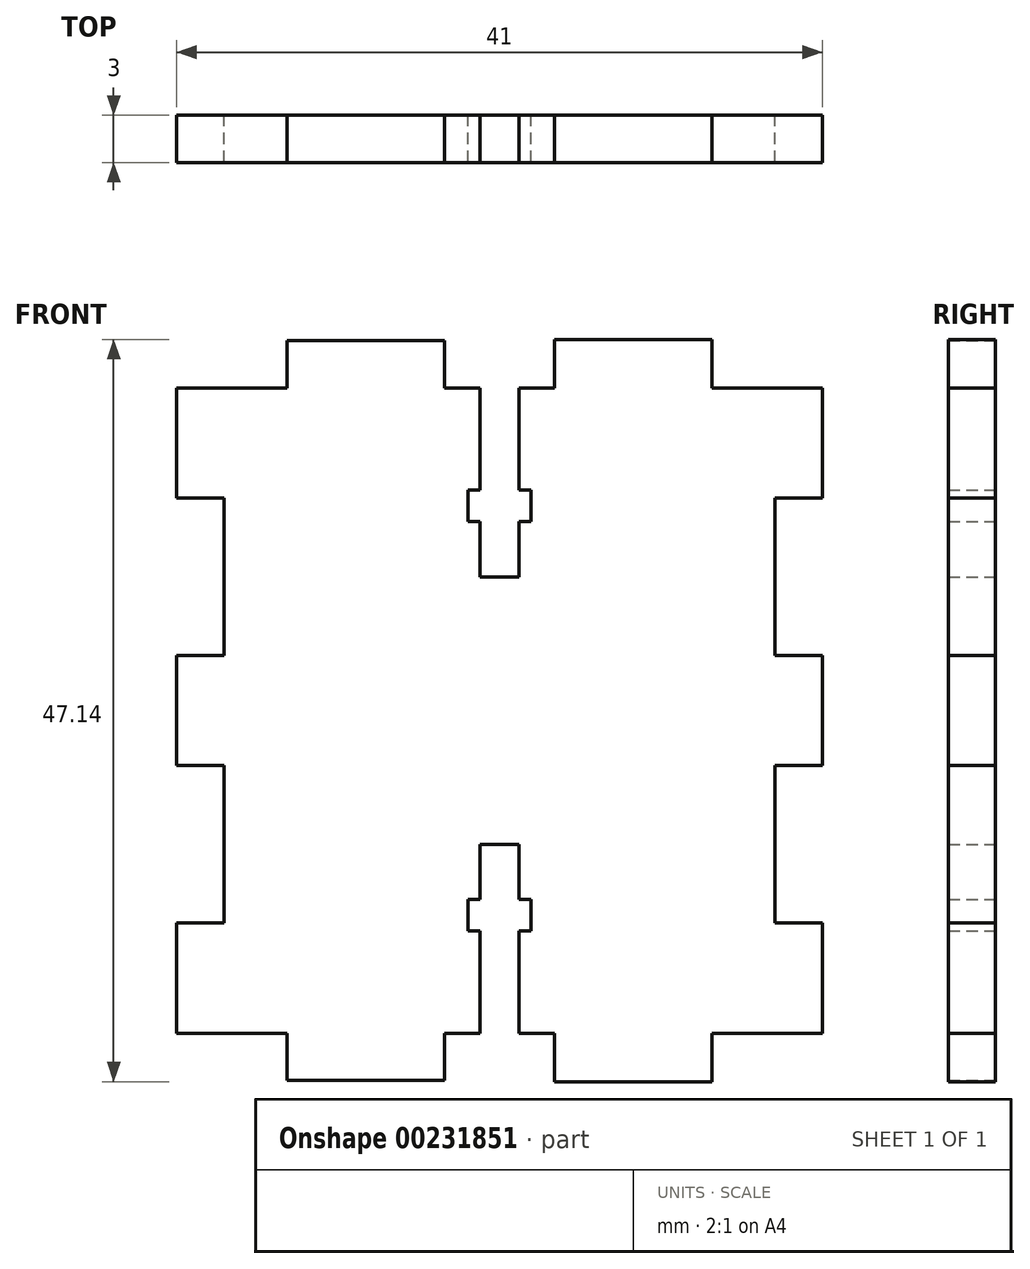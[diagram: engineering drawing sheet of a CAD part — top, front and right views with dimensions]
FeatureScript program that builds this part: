
annotation { "Feature Type Name" : "Feature", "Feature Type Description" : "" }
export const myFeature = defineFeature(function(context is Context, id is Id, definition is map)
    precondition{}
    {
        {
            var Q0;
            Q0=qCreatedBy(makeId("Front.planeOp"),FACE);
            var sketch = newSketch(context, id + "F0", { "sketchPlane" : qUnion([Q0])});
            skLineSegment(sketch, "E0", {"start": v(0, 0) * mm, "end": v(7, 0) * mm});
            skLineSegment(sketch, "E1", {"start": v(7, 0) * mm, "end": v(7, 3) * mm});
            skLineSegment(sketch, "E2", {"start": v(7, 3) * mm, "end": v(17, 3) * mm});
            skLineSegment(sketch, "E3", {"start": v(17, 3) * mm, "end": v(17, 0) * mm});
            skLineSegment(sketch, "E4", {"start": v(17, 0) * mm, "end": v(19.25, 0) * mm});
            skLineSegment(sketch, "E5", {"start": v(24, 0) * mm, "end": v(24, 3.07) * mm});
            skLineSegment(sketch, "E6", {"start": v(24, 3.07) * mm, "end": v(34, 3.07) * mm});
            skLineSegment(sketch, "E7", {"start": v(34, 3.07) * mm, "end": v(34, 0) * mm});
            skLineSegment(sketch, "E8", {"start": v(34, 0) * mm, "end": v(41, 0) * mm});
            skLineSegment(sketch, "E9", {"start": v(41, -20.5) * mm, "end": v(0, -20.5) * mm, "construction": true});
            skLineSegment(sketch, "E10.top", {"start": v(19.25, -12) * mm, "end": v(21.75, -12) * mm});
            skLineSegment(sketch, "E10.left", {"start": v(19.25, 0) * mm, "end": v(19.25, -6.5) * mm});
            skLineSegment(sketch, "E10.right", {"start": v(21.75, 0) * mm, "end": v(21.75, -6.5) * mm});
            skLineSegment(sketch, "E11.bottom", {"start": v(18.5, -8.5) * mm, "end": v(19.25, -8.5) * mm});
            skLineSegment(sketch, "E11.top", {"start": v(18.5, -6.5) * mm, "end": v(19.25, -6.5) * mm});
            skLineSegment(sketch, "E11.left", {"start": v(18.5, -8.5) * mm, "end": v(18.5, -6.5) * mm});
            skLineSegment(sketch, "E11.right", {"start": v(22.5, -8.5) * mm, "end": v(22.5, -6.5) * mm});
            skLineSegment(sketch, "E12.trimOffspring", {"start": v(21.75, -6.5) * mm, "end": v(22.5, -6.5) * mm});
            skLineSegment(sketch, "E13.trimOffspring", {"start": v(21.75, -8.5) * mm, "end": v(21.75, -12) * mm});
            skLineSegment(sketch, "E14.trimOffspring", {"start": v(19.25, -8.5) * mm, "end": v(19.25, -12) * mm});
            skLineSegment(sketch, "E15.trimOffspring", {"start": v(21.75, -8.5) * mm, "end": v(22.5, -8.5) * mm});
            skLineSegment(sketch, "E16.trimOffspring", {"start": v(21.75, 0) * mm, "end": v(24, 0) * mm});
            skLineSegment(sketch, "E17.MirrorCS", {"start": v(18.5, -34.5) * mm, "end": v(19.25, -34.5) * mm});
            skLineSegment(sketch, "E18.MirrorCS", {"start": v(22.5, -32.5) * mm, "end": v(22.5, -34.5) * mm});
            skLineSegment(sketch, "E19.MirrorCS", {"start": v(34, -44.07) * mm, "end": v(34, -41) * mm});
            skLineSegment(sketch, "E20.MirrorCS", {"start": v(17, -44) * mm, "end": v(17, -41) * mm});
            skLineSegment(sketch, "E21.MirrorCS", {"start": v(21.75, -41) * mm, "end": v(24, -41) * mm});
            skLineSegment(sketch, "E22.MirrorCS", {"start": v(19.25, -29) * mm, "end": v(21.75, -29) * mm});
            skLineSegment(sketch, "E23.MirrorCS", {"start": v(17, -41) * mm, "end": v(19.25, -41) * mm});
            skLineSegment(sketch, "E24.MirrorCS", {"start": v(24, -41) * mm, "end": v(24, -44.07) * mm});
            skLineSegment(sketch, "E25.MirrorCS", {"start": v(18.5, -32.5) * mm, "end": v(19.25, -32.5) * mm});
            skLineSegment(sketch, "E26.MirrorCS", {"start": v(7, -41) * mm, "end": v(7, -44) * mm});
            skLineSegment(sketch, "E27.MirrorCS", {"start": v(21.75, -32.5) * mm, "end": v(22.5, -32.5) * mm});
            skLineSegment(sketch, "E28.MirrorCS", {"start": v(21.75, -34.5) * mm, "end": v(22.5, -34.5) * mm});
            skLineSegment(sketch, "E29.MirrorCS", {"start": v(18.5, -32.5) * mm, "end": v(18.5, -34.5) * mm});
            skLineSegment(sketch, "E30.MirrorCS", {"start": v(24, -44.07) * mm, "end": v(34, -44.07) * mm});
            skLineSegment(sketch, "E31.MirrorCS", {"start": v(19.25, -41) * mm, "end": v(19.25, -34.5) * mm});
            skLineSegment(sketch, "E32.MirrorCS", {"start": v(0, -41) * mm, "end": v(7, -41) * mm});
            skLineSegment(sketch, "E33.MirrorCS", {"start": v(21.75, -32.5) * mm, "end": v(21.75, -29) * mm});
            skLineSegment(sketch, "E34.MirrorCS", {"start": v(19.25, -32.5) * mm, "end": v(19.25, -29) * mm});
            skLineSegment(sketch, "E35.MirrorCS", {"start": v(7, -44) * mm, "end": v(17, -44) * mm});
            skLineSegment(sketch, "E36.MirrorCS", {"start": v(34, -41) * mm, "end": v(41, -41) * mm});
            skLineSegment(sketch, "E37.MirrorCS", {"start": v(21.75, -41) * mm, "end": v(21.75, -34.5) * mm});
            skLineSegment(sketch, "E38", {"start": v(20.5, -29) * mm, "end": v(20.5, 3.72) * mm, "construction": true});
            skPoint(sketch, "E39.MirrorCS.start.orphan", {"position": v(0, -20.5) * mm});
            skPoint(sketch, "E40.MirrorCS.end.orphan", {"position": v(41, -20.5) * mm});
            skLineSegment(sketch, "E41", {"start": v(41, 0) * mm, "end": v(41, -7) * mm});
            skLineSegment(sketch, "E42", {"start": v(41, -7) * mm, "end": v(38, -7) * mm});
            skLineSegment(sketch, "E43", {"start": v(38, -7) * mm, "end": v(38, -17) * mm});
            skLineSegment(sketch, "E44", {"start": v(38, -17) * mm, "end": v(41, -17) * mm});
            skLineSegment(sketch, "E45", {"start": v(41, -17) * mm, "end": v(41, -24) * mm});
            skLineSegment(sketch, "E46", {"start": v(41, -24) * mm, "end": v(38, -24) * mm});
            skLineSegment(sketch, "E47", {"start": v(38, -24) * mm, "end": v(38, -34) * mm});
            skLineSegment(sketch, "E48", {"start": v(38, -34) * mm, "end": v(41, -34) * mm});
            skLineSegment(sketch, "E49", {"start": v(41, -34) * mm, "end": v(41, -41) * mm});
            skLineSegment(sketch, "E50.MirrorCS", {"start": v(0, -24) * mm, "end": v(3, -24) * mm});
            skLineSegment(sketch, "E51.MirrorCS", {"start": v(0, -7) * mm, "end": v(3, -7) * mm});
            skLineSegment(sketch, "E52.MirrorCS", {"start": v(3, -34) * mm, "end": v(0, -34) * mm});
            skLineSegment(sketch, "E53.MirrorCS", {"start": v(0, -17) * mm, "end": v(0, -24) * mm});
            skLineSegment(sketch, "E54.MirrorCS", {"start": v(3, -17) * mm, "end": v(0, -17) * mm});
            skLineSegment(sketch, "E55.MirrorCS", {"start": v(0, -34) * mm, "end": v(0, -41) * mm});
            skLineSegment(sketch, "E56.MirrorCS", {"start": v(3, -7) * mm, "end": v(3, -17) * mm});
            skLineSegment(sketch, "E57.MirrorCS", {"start": v(0, 0) * mm, "end": v(0, -7) * mm});
            skLineSegment(sketch, "E58.MirrorCS", {"start": v(3, -24) * mm, "end": v(3, -34) * mm});
            skSolve(sketch);
        }
        {
            var Q0;
            Q0=qSketchRegion(id+"F0",true);
            extrude(context, id + "F1", {"entities" : qUnion([Q0]), "endBound" : BoundingType.SYMMETRIC, "depth" : 3 * mm});
        }
    });
